# Revit family: 11837,002
name_source: partatom
category: Plumbing Fixtures
revit_build: Autodesk Revit 2018 (Build: 22.0.11200.0000)
units: mm (PartAtom-declared; Revit-internal decimal feet)

## family parameters
Always vertical = Yes
Cut with Voids When Loaded = No
OmniClass Number = 23.45.30.14.11
OmniClass Title = Commercial Dishwashers
Part Type = Normal
Room Calculation Point = No
Round Connector Dimension = Use Diameter
Shared = No
Work Plane-Based = No

## types (1)
- Standard
    CW Connection = No
    Connector_2_Diameter = 0 mm  [stored 0 ft]
    Connector_3_Diameter = 0 mm  [stored 0 ft]
    Description = Tray dishwasher
    HW Connection = No
    Manufacturer = Wexiödisk AB
    Model = WD-215T V-H
    URL = www.wexiodisk.com
    Vent Connection = No
    Waste Connection = No

note: [stored X ft] marks values corroborated as IEEE doubles in the binary element streams (Revit-internal decimal feet)

## geometry (parser evidence)
native form markers: Sweep x2
no freeform markers — native parametric forms only
